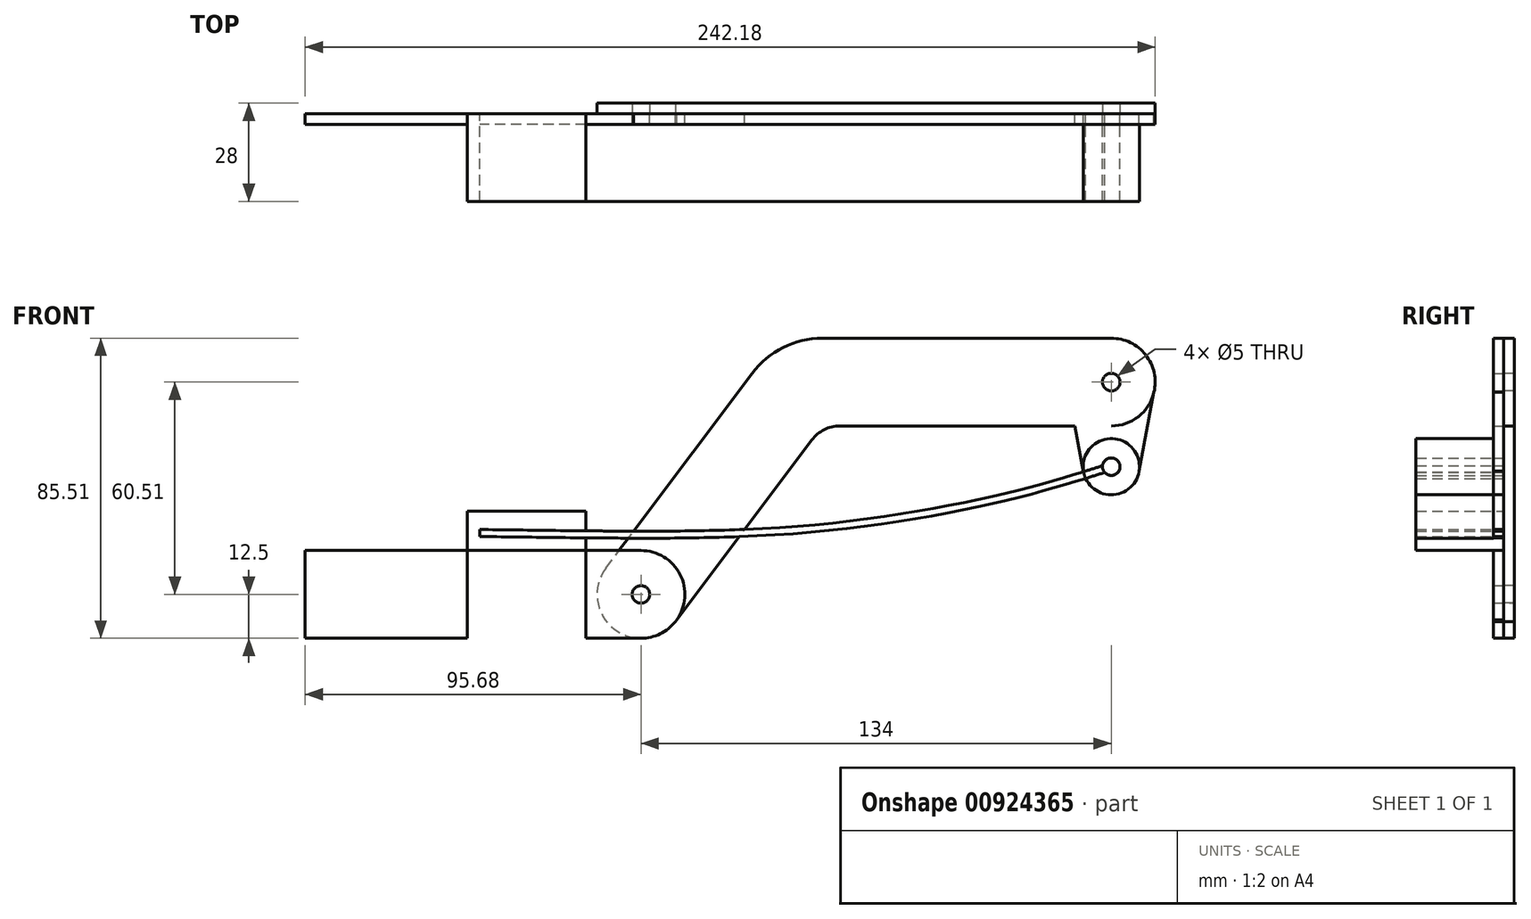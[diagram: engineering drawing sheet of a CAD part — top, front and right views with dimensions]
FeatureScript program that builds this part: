
annotation { "Feature Type Name" : "Feature", "Feature Type Description" : "" }
export const myFeature = defineFeature(function(context is Context, id is Id, definition is map)
    precondition{}
    {
        {
            var Q0;
            Q0=qCreatedBy(makeId("Front.planeOp"),FACE);
            var sketch = newSketch(context, id + "F0", { "sketchPlane" : qUnion([Q0])});
            skCircle(sketch, "E0", {"center": v(0, 0) * mm, "radius": 12.5 * mm});
            skLineSegment(sketch, "E1", {"start": v(0, 12.5) * mm, "end": v(-95.68, 12.5) * mm});
            skLineSegment(sketch, "E2", {"start": v(0, -12.5) * mm, "end": v(-95.68, -12.5) * mm});
            skLineSegment(sketch, "E3", {"start": v(-95.68, 12.5) * mm, "end": v(-95.68, -12.5) * mm});
            skLineSegment(sketch, "E4", {"start": v(-10, 7.5) * mm, "end": v(31.68, 63.02) * mm});
            skLineSegment(sketch, "E5", {"start": v(51.67, 73.01) * mm, "end": v(134, 73.01) * mm});
            skCircle(sketch, "E6", {"center": v(134, 60.51) * mm, "radius": 12.5 * mm});
            skPoint(sketch, "E7.visualSharp", {"position": v(39.18, 73.01) * mm});
            skArc(sketch, "E7.filletArc", {"start": v(51.67, 73.01) * mm, "mid": v(40.5, 70.38) * mm, "end": v(31.68, 63.02) * mm});
            skLineSegment(sketch, "E8.0", {"start": v(56.67, 48.01) * mm, "end": v(134, 48.01) * mm});
            skLineSegment(sketch, "E8.1", {"start": v(9.32, -8.4) * mm, "end": v(48.67, 44.02) * mm});
            skArc(sketch, "E9.filletArc", {"start": v(56.67, 48.01) * mm, "mid": v(52.2, 46.96) * mm, "end": v(48.67, 44.02) * mm});
            skLineSegment(sketch, "E10", {"start": v(134, 60.51) * mm, "end": v(134, 22.68) * mm, "construction": true});
            skCircle(sketch, "E11", {"center": v(134, 36.4) * mm, "radius": 8.02 * mm});
            skLineSegment(sketch, "E12", {"start": v(126.1, 34.92) * mm, "end": v(121.7, 58.2) * mm});
            skLineSegment(sketch, "E13", {"start": v(141.88, 34.92) * mm, "end": v(146.27, 58.2) * mm});
            skCircle(sketch, "E14", {"center": v(0, 0) * mm, "radius": 2.5 * mm});
            skCircle(sketch, "E15", {"center": v(134, 60.51) * mm, "radius": 2.5 * mm});
            skCircle(sketch, "E16", {"center": v(134, 36.4) * mm, "radius": 2.5 * mm});
            skFitSpline(sketch, "E17", {"points": [v(134, 36.4) * mm, v(-45.92, 17.5) * mm], "startDerivative": vector(-158.03, -46.16) * mm, "endDerivative": vector(-193.27, 2.38) * mm, "construction": true});
            skFitSpline(sketch, "E18.0", {"points": [v(133.71, 37.37) * mm, v(107.45, 29.7) * mm, v(49.83, 19.86) * mm, v(-13.72, 18.1) * mm, v(-45.9, 18.5) * mm]});
            skLineSegment(sketch, "E19", {"start": v(-45.9, 18.5) * mm, "end": v(-45.93, 16.5) * mm});
            skLineSegment(sketch, "E20.bottom", {"start": v(-49.48, 23.74) * mm, "end": v(-15.67, 23.74) * mm});
            skLineSegment(sketch, "E20.top", {"start": v(-49.48, -12.5) * mm, "end": v(-15.67, -12.5) * mm});
            skLineSegment(sketch, "E20.left", {"start": v(-49.48, 23.74) * mm, "end": v(-49.48, -12.5) * mm});
            skLineSegment(sketch, "E20.right", {"start": v(-15.67, 23.74) * mm, "end": v(-15.67, -12.5) * mm});
            skLineSegment(sketch, "E21", {"start": v(131.61, 34.68) * mm, "end": v(130.97, 36.58) * mm});
            skFitSpline(sketch, "E22.trimOffspring", {"points": [v(134.27, 35.45) * mm, v(107.85, 27.73) * mm, v(50, 17.86) * mm, v(-13.69, 16.1) * mm, v(-45.93, 16.5) * mm]});
            skSolve(sketch);
        }
        {
            var Q0;
            {var subQ0=sQuery(id+"F0.wireOp",EDGE,"E3");Q0=makeQuery(id+"F0.imprint","IMPRINT",FACE,{"disambiguationData":[TD([[makeQuery(id+"F0.imprint","IMPRINT",EDGE,{"derivedFrom":subQ0}),1.0]])]});}
            var Q1;
            {var subQ5=sQuery(id+"F0.wireOp",EDGE,"E20.top");Q1=makeQuery(id+"F0.imprint","IMPRINT",FACE,{"disambiguationData":[TD([[makeQuery(id+"F0.imprint","IMPRINT",EDGE,{"derivedFrom":subQ5}),1.0]])]});}
            var Q2;
            {var subQ0=sQuery(id+"F0.wireOp",EDGE,"E2");var subQ1=sQuery(id+"F0.wireOp",EDGE,"E0");var subQ2=makeQuery(id+"F0.imprint","INTERSECT",VERTEX,{"derivedFrom":[subQ1,subQ0]});Q2=makeQuery(id+"F0.imprint","IMPRINT",FACE,{"disambiguationData":[TD([[makeQuery(id+"F0.imprint","IMPRINT",EDGE,{"disambiguationData":[TD([[subQ2,1.0]])],"derivedFrom":subQ1}),-1.0]])]});}
            var Q3;
            {var subQ0=sQuery(id+"F0.wireOp",EDGE,"E1");var subQ1=sQuery(id+"F0.wireOp",EDGE,"E0");var subQ2=makeQuery(id+"F0.imprint","INTERSECT",VERTEX,{"derivedFrom":[subQ1,subQ0]});Q3=makeQuery(id+"F0.imprint","IMPRINT",FACE,{"disambiguationData":[TD([[makeQuery(id+"F0.imprint","IMPRINT",EDGE,{"disambiguationData":[TD([[subQ2,-1.0]])],"derivedFrom":subQ1}),-1.0]])]});}
            var Q4;
            Q4=makeQuery(id+"F0.imprint","IMPRINT",FACE,{"disambiguationData":[TD([[makeQuery(id+"F0.imprint","IMPRINT",EDGE,{"derivedFrom":sQuery(id+"F0.wireOp",EDGE,"E14")}),-1.0]])]});
            extrude(context, id + "F1", {"entities" : qUnion([Q0, Q1, Q2, Q3, Q4]), "depth" : 3 * mm, "offsetDistance" : 25 * mm});
        }
        {
            var Q0;
            {var subQ1=sQuery(id+"F0.wireOp",EDGE,"E5");Q0=makeQuery(id+"F0.imprint","IMPRINT",FACE,{"disambiguationData":[TD([[makeQuery(id+"F0.imprint","IMPRINT",EDGE,{"derivedFrom":subQ1}),-1.0]])]});}
            var Q1;
            {var subQ0=sQuery(id+"F0.wireOp",EDGE,"E18.0");var subQ1=sQuery(id+"F0.wireOp",EDGE,"E4");var subQ2=makeQuery(id+"F0.imprint","INTERSECT",VERTEX,{"derivedFrom":[subQ1,subQ0]});Q1=makeQuery(id+"F0.imprint","IMPRINT",FACE,{"disambiguationData":[TD([[makeQuery(id+"F0.imprint","IMPRINT",EDGE,{"disambiguationData":[TD([[subQ2,1.0]])],"derivedFrom":subQ1}),-1.0]])]});}
            var Q2;
            {var subQ1=sQuery(id+"F0.wireOp",EDGE,"E1");var subQ6=sQuery(id+"F0.wireOp",EDGE,"E0");var subQ9=makeQuery(id+"F0.imprint","INTERSECT",VERTEX,{"derivedFrom":[subQ6,subQ1]});Q2=makeQuery(id+"F0.imprint","IMPRINT",FACE,{"disambiguationData":[TD([[makeQuery(id+"F0.imprint","IMPRINT",EDGE,{"disambiguationData":[TD([[subQ9,1.0]])],"derivedFrom":subQ6}),-1.0]])]});}
            var Q3;
            Q3=makeQuery(id+"F0.imprint","IMPRINT",FACE,{"disambiguationData":[TD([[makeQuery(id+"F0.imprint","IMPRINT",EDGE,{"derivedFrom":sQuery(id+"F0.wireOp",EDGE,"E14")}),-1.0]])]});
            var Q4;
            {var subQ0=sQuery(id+"F0.wireOp",EDGE,"E1");var subQ1=sQuery(id+"F0.wireOp",EDGE,"E0");var subQ2=makeQuery(id+"F0.imprint","INTERSECT",VERTEX,{"derivedFrom":[subQ1,subQ0]});Q4=makeQuery(id+"F0.imprint","IMPRINT",FACE,{"disambiguationData":[TD([[makeQuery(id+"F0.imprint","IMPRINT",EDGE,{"disambiguationData":[TD([[subQ2,-1.0]])],"derivedFrom":subQ1}),-1.0]])]});}
            var Q5;
            Q5=makeQuery(id+"F0.imprint","IMPRINT",FACE,{"disambiguationData":[TD([[makeQuery(id+"F0.imprint","IMPRINT",EDGE,{"derivedFrom":sQuery(id+"F0.wireOp",EDGE,"E15")}),-1.0]])]});
            var Q6;
            {var subQ0=sQuery(id+"F0.wireOp",EDGE,"E8.0");var subQ1=sQuery(id+"F0.wireOp",EDGE,"E6");var subQ2=makeQuery(id+"F0.imprint","INTERSECT",VERTEX,{"derivedFrom":[subQ1,subQ0]});Q6=makeQuery(id+"F0.imprint","IMPRINT",FACE,{"disambiguationData":[TD([[makeQuery(id+"F0.imprint","IMPRINT",EDGE,{"disambiguationData":[TD([[subQ2,1.0]])],"derivedFrom":subQ1}),-1.0]])]});}
            extrude(context, id + "F2", {"entities" : qUnion([Q0, Q1, Q2, Q3, Q4, Q5, Q6]), "oppositeDirection" : true, "depth" : 3 * mm, "offsetDistance" : 25 * mm});
        }
        {
            var Q0;
            {var subQ0=sQuery(id+"F0.wireOp",EDGE,"E13");Q0=makeQuery(id+"F0.imprint","IMPRINT",FACE,{"disambiguationData":[TD([[makeQuery(id+"F0.imprint","IMPRINT",EDGE,{"derivedFrom":subQ0}),1.0]])]});}
            var Q1;
            Q1=makeQuery(id+"F0.imprint","IMPRINT",FACE,{"disambiguationData":[TD([[makeQuery(id+"F0.imprint","IMPRINT",EDGE,{"derivedFrom":sQuery(id+"F0.wireOp",EDGE,"E15")}),-1.0]])]});
            var Q2;
            {var subQ0=sQuery(id+"F0.wireOp",EDGE,"E8.0");var subQ1=sQuery(id+"F0.wireOp",EDGE,"E6");var subQ2=makeQuery(id+"F0.imprint","INTERSECT",VERTEX,{"derivedFrom":[subQ1,subQ0]});Q2=makeQuery(id+"F0.imprint","IMPRINT",FACE,{"disambiguationData":[TD([[makeQuery(id+"F0.imprint","IMPRINT",EDGE,{"disambiguationData":[TD([[subQ2,1.0]])],"derivedFrom":subQ1}),-1.0]])]});}
            var Q3;
            {var subQ5=sQuery(id+"F0.wireOp",EDGE,"E11");var subQ7=makeQuery(id+"F0.imprint","INTERSECT",VERTEX,{"derivedFrom":[subQ5,sQuery(id+"F0.wireOp",EDGE,"E13")]});Q3=makeQuery(id+"F0.imprint","IMPRINT",FACE,{"disambiguationData":[TD([[makeQuery(id+"F0.imprint","IMPRINT",EDGE,{"disambiguationData":[TD([[subQ7,1.0]])],"derivedFrom":subQ5}),1.0]])]});}
            var Q4;
            {var subQ1=sQuery(id+"F0.wireOp",EDGE,"E11");var subQ5=makeQuery(id+"F0.imprint","INTERSECT",VERTEX,{"derivedFrom":[subQ1,sQuery(id+"F0.wireOp",EDGE,"E12")]});Q4=makeQuery(id+"F0.imprint","IMPRINT",FACE,{"disambiguationData":[TD([[makeQuery(id+"F0.imprint","IMPRINT",EDGE,{"disambiguationData":[TD([[subQ5,1.0]])],"derivedFrom":subQ1}),1.0]])]});}
            extrude(context, id + "F3", {"entities" : qUnion([Q0, Q1, Q2, Q3, Q4]), "depth" : 3 * mm, "offsetDistance" : 25 * mm});
        }
        {
            var Q0;
            {var subQ5=sQuery(id+"F0.wireOp",EDGE,"E11");var subQ7=makeQuery(id+"F0.imprint","INTERSECT",VERTEX,{"derivedFrom":[subQ5,sQuery(id+"F0.wireOp",EDGE,"E13")]});Q0=makeQuery(id+"F0.imprint","IMPRINT",FACE,{"disambiguationData":[TD([[makeQuery(id+"F0.imprint","IMPRINT",EDGE,{"disambiguationData":[TD([[subQ7,1.0]])],"derivedFrom":subQ5}),1.0]])]});}
            extrude(context, id + "F4", {"entities" : qUnion([Q0]), "depth" : 25 * mm, "offsetDistance" : 25 * mm, "hasSecondDirection" : true, "secondDirectionOppositeDirection" : false, "secondDirectionDepth" : 3 * mm});
        }
        {
            var Q0;
            {var subQ0=sQuery(id+"F0.wireOp",EDGE,"E19");Q0=makeQuery(id+"F0.imprint","IMPRINT",FACE,{"disambiguationData":[TD([[makeQuery(id+"F0.imprint","IMPRINT",EDGE,{"derivedFrom":subQ0}),-1.0]])]});}
            var Q1;
            {var subQ5=sQuery(id+"F0.wireOp",EDGE,"E20.top");Q1=makeQuery(id+"F0.imprint","IMPRINT",FACE,{"disambiguationData":[TD([[makeQuery(id+"F0.imprint","IMPRINT",EDGE,{"derivedFrom":subQ5}),1.0]])]});}
            extrude(context, id + "F5", {"entities" : qUnion([Q0, Q1]), "operationType" : NewBodyOperationType.ADD, "depth" : 25 * mm, "offsetDistance" : 25 * mm});
        }
        {
            var Q0;
            {var subQ0=sQuery(id+"F0.wireOp",EDGE,"E18.0");var subQ1=sQuery(id+"F0.wireOp",EDGE,"E4");var subQ2=makeQuery(id+"F0.imprint","INTERSECT",VERTEX,{"derivedFrom":[subQ1,subQ0]});Q0=makeQuery(id+"F0.imprint","IMPRINT",FACE,{"disambiguationData":[TD([[makeQuery(id+"F0.imprint","IMPRINT",EDGE,{"disambiguationData":[TD([[subQ2,1.0]])],"derivedFrom":subQ1}),-1.0]])]});}
            var Q1;
            {var subQ0=sQuery(id+"F0.wireOp",EDGE,"E19");Q1=makeQuery(id+"F0.imprint","IMPRINT",FACE,{"disambiguationData":[TD([[makeQuery(id+"F0.imprint","IMPRINT",EDGE,{"derivedFrom":subQ0}),1.0]])]});}
            var Q2;
            {var subQ0=sQuery(id+"F0.wireOp",EDGE,"E18.0");var subQ1=sQuery(id+"F0.wireOp",EDGE,"E4");var subQ2=makeQuery(id+"F0.imprint","INTERSECT",VERTEX,{"derivedFrom":[subQ1,subQ0]});Q2=makeQuery(id+"F0.imprint","IMPRINT",FACE,{"disambiguationData":[TD([[makeQuery(id+"F0.imprint","IMPRINT",EDGE,{"disambiguationData":[TD([[subQ2,1.0]])],"derivedFrom":subQ1}),1.0]])]});}
            var Q3;
            {var subQ1=sQuery(id+"F0.wireOp",EDGE,"E11");var subQ5=makeQuery(id+"F0.imprint","INTERSECT",VERTEX,{"derivedFrom":[subQ1,sQuery(id+"F0.wireOp",EDGE,"E12")]});Q3=makeQuery(id+"F0.imprint","IMPRINT",FACE,{"disambiguationData":[TD([[makeQuery(id+"F0.imprint","IMPRINT",EDGE,{"disambiguationData":[TD([[subQ5,1.0]])],"derivedFrom":subQ1}),1.0]])]});}
            var Q4;
            {var subQ1=sQuery(id+"F0.wireOp",EDGE,"E8.1");var subQ7=sQuery(id+"F0.wireOp",EDGE,"E22.trimOffspring");var subQ9=makeQuery(id+"F0.imprint","INTERSECT",VERTEX,{"derivedFrom":[subQ1,subQ7]});Q4=makeQuery(id+"F0.imprint","IMPRINT",FACE,{"disambiguationData":[TD([[makeQuery(id+"F0.imprint","IMPRINT",EDGE,{"disambiguationData":[TD([[subQ9,-1.0]])],"derivedFrom":subQ1}),-1.0]])]});}
            extrude(context, id + "F6", {"entities" : qUnion([Q0, Q1, Q2, Q3, Q4]), "depth" : 25 * mm, "offsetDistance" : 25 * mm, "hasSecondDirection" : true, "secondDirectionOppositeDirection" : false, "secondDirectionDepth" : 3 * mm});
        }
        {
            var Q0;
            Q0=makeQuery(id+"F0.imprint","IMPRINT",FACE,{"disambiguationData":[TD([[makeQuery(id+"F0.imprint","IMPRINT",EDGE,{"derivedFrom":sQuery(id+"F0.wireOp",EDGE,"E14")}),1.0]])]});
            extrude(context, id + "F7", {"entities" : qUnion([Q0]), "endBound" : BoundingType.SYMMETRIC, "depth" : 6 * mm, "offsetDistance" : 25 * mm});
        }
        {
            var Q0;
            Q0=makeQuery(id+"F0.imprint","IMPRINT",FACE,{"disambiguationData":[TD([[makeQuery(id+"F0.imprint","IMPRINT",EDGE,{"derivedFrom":sQuery(id+"F0.wireOp",EDGE,"E16")}),1.0]])]});
            extrude(context, id + "F8", {"entities" : qUnion([Q0]), "depth" : 25 * mm, "offsetDistance" : 25 * mm, "hasSecondDirection" : true, "secondDirectionOppositeDirection" : true, "secondDirectionDepth" : 0 * mm});
        }
    });
